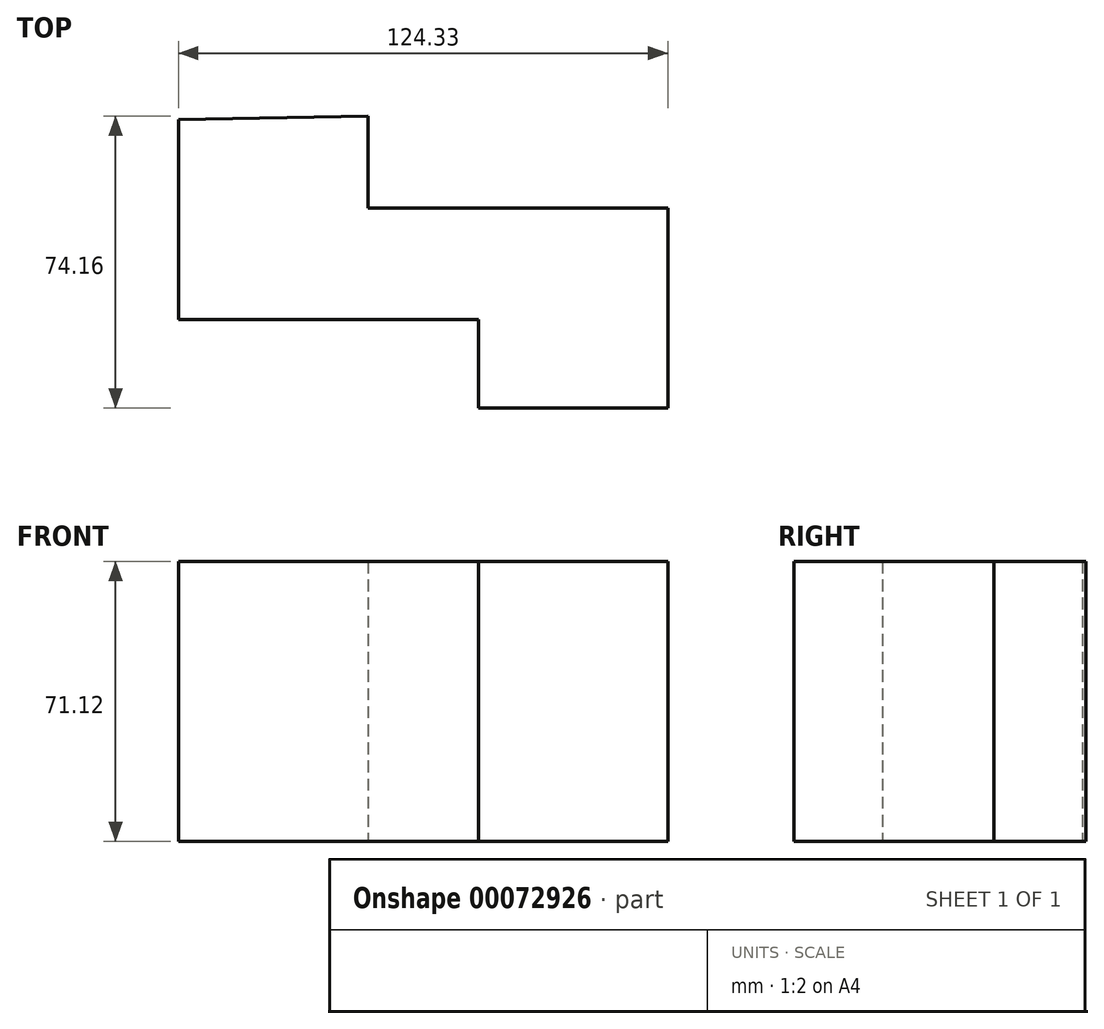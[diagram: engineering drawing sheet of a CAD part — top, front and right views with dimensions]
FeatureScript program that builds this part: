
annotation { "Feature Type Name" : "Feature", "Feature Type Description" : "" }
export const myFeature = defineFeature(function(context is Context, id is Id, definition is map)
    precondition{}
    {
        {
            var Q0;
            Q0=qCreatedBy(makeId("Top.planeOp"),FACE);
            var sketch = newSketch(context, id + "F0", { "sketchPlane" : qUnion([Q0])});
            skLineSegment(sketch, "E0", {"start": v(-93.16, 50.8) * mm, "end": v(-93.16, 0) * mm});
            skLineSegment(sketch, "E1", {"start": v(-93.16, 0) * mm, "end": v(-16.96, 0) * mm});
            skLineSegment(sketch, "E2", {"start": v(-16.96, 0) * mm, "end": v(-16.96, -22.52) * mm});
            skLineSegment(sketch, "E3", {"start": v(-16.96, -22.52) * mm, "end": v(31.17, -22.52) * mm});
            skLineSegment(sketch, "E4", {"start": v(31.17, -22.52) * mm, "end": v(31.17, 28.28) * mm});
            skLineSegment(sketch, "E5", {"start": v(31.17, 28.28) * mm, "end": v(-45.03, 28.28) * mm});
            skLineSegment(sketch, "E6", {"start": v(-45.03, 28.28) * mm, "end": v(-45.03, 51.64) * mm});
            skLineSegment(sketch, "E7", {"start": v(-45.03, 51.64) * mm, "end": v(-93.16, 50.8) * mm});
            skSolve(sketch);
        }
        {
            var Q0;
            Q0 = qSketchRegion(id + "F0", true);
            extrude(context, id + "F1", {"entities" : qUnion([Q0]), "depth" : 71.12 * mm});
        }
    });
